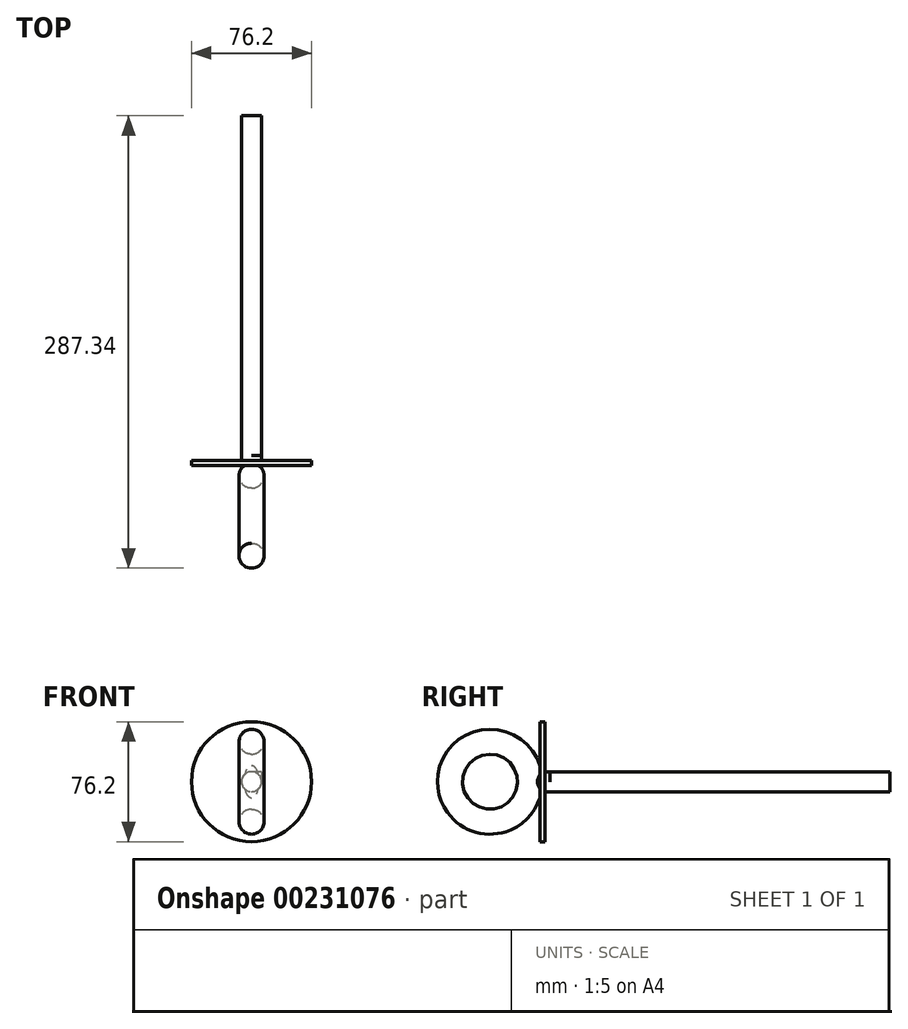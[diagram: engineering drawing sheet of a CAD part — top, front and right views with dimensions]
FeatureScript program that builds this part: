
annotation { "Feature Type Name" : "Feature", "Feature Type Description" : "" }
export const myFeature = defineFeature(function(context is Context, id is Id, definition is map)
    precondition{}
    {
        {
            var Q0;
            Q0=qCreatedBy(makeId("Front.planeOp"),FACE);
            var sketch = newSketch(context, id + "F0", { "sketchPlane" : qUnion([Q0])});
            skLineSegment(sketch, "E0", {"start": v(0, 0) * mm, "end": v(27.89, 0) * mm, "construction": true});
            skCircle(sketch, "E1", {"center": v(7.94, 25.4) * mm, "radius": 7.94 * mm});
            skSolve(sketch);
        }
        {
            var Q0;
            Q0 = qSketchRegion(id + "F0", true);
            var Q1;
            Q1=sQuery(id+"F0.wireOp",EDGE,"E0");
            revolve(context, id + "F1", {"entities" : qUnion([Q0]), "axis" : qUnion([Q1]), "revolveType" : RevolveType.FULL});
        }
        {
            var Q0;
            Q0=qCreatedBy(makeId("Front.planeOp"),FACE);
            cPlane(context, id + "F2", {"entities" : qUnion([Q0]), "cplaneType" : CPlaneType.OFFSET, "offset" : 254 * mm, "oppositeDirection" : true, "width" : 152.4 * mm, "height" : 152.4 * mm});
        }
        {
            var Q0;
            Q0=qCreatedBy(id+"F2.planeOp",FACE);
            var sketch = newSketch(context, id + "F3", { "sketchPlane" : qUnion([Q0])});
            skCircle(sketch, "E2", {"center": v(7.94, 0) * mm, "radius": 6.35 * mm});
            skSolve(sketch);
        }
        {
            var Q0;
            Q0 = qSketchRegion(id + "F3", true);
            var Q1;
            Q1=makeQuery(id+"F1.opRevolve","SWEPT_FACE",FACE,{"disambiguationData":[OSD([sQuery(id+"F0.wireOp",EDGE,"E1")])]});
            extrude(context, id + "F4", {"entities" : qUnion([Q0]), "operationType" : NewBodyOperationType.ADD, "endBound" : BoundingType.UP_TO_SURFACE, "endBoundEntityFace" : qUnion([Q1]), "depth" : 25.4 * mm});
        }
        {
            var Q0;
            Q0=qCreatedBy(makeId("Front.planeOp"),FACE);
            cPlane(context, id + "F5", {"entities" : qUnion([Q0]), "cplaneType" : CPlaneType.OFFSET, "offset" : 31.75 * mm, "oppositeDirection" : true, "width" : 152.4 * mm, "height" : 152.4 * mm});
        }
        {
            var Q0;
            Q0=qCreatedBy(id+"F5.planeOp",FACE);
            var sketch = newSketch(context, id + "F6", { "sketchPlane" : qUnion([Q0])});
            skCircle(sketch, "E3", {"center": v(7.94, 0) * mm, "radius": 38.1 * mm});
            skSolve(sketch);
        }
        {
            var Q0;
            Q0 = qSketchRegion(id + "F6", true);
            extrude(context, id + "F7", {"entities" : qUnion([Q0]), "operationType" : NewBodyOperationType.ADD, "oppositeDirection" : true, "depth" : 3.17 * mm});
        }
        {
            var Q0;
            Q0=makeQuery(id+"F7.opExtrude","CAP_FACE",FACE,{"disambiguationData":[OSD([sQuery(id+"F6.wireOp",EDGE,"E3")])],"isStart":false});
            var sketch = newSketch(context, id + "F8", { "sketchPlane" : qUnion([Q0])});
            skLineSegment(sketch, "E4.bottom", {"start": v(-14.29, 6.35) * mm, "end": v(-7.94, 6.35) * mm});
            skLineSegment(sketch, "E4.left", {"start": v(-14.29, 6.35) * mm, "end": v(-14.29, 0) * mm});
            skLineSegment(sketch, "E5", {"start": v(-14.29, 0) * mm, "end": v(-7.94, 0) * mm});
            skLineSegment(sketch, "E6", {"start": v(-7.94, 0) * mm, "end": v(-7.94, 6.35) * mm});
            skSolve(sketch);
        }
        {
            var Q0;
            Q0 = qSketchRegion(id + "F8", true);
            extrude(context, id + "F9", {"entities" : qUnion([Q0]), "operationType" : NewBodyOperationType.ADD, "depth" : 3.17 * mm});
        }
    });
